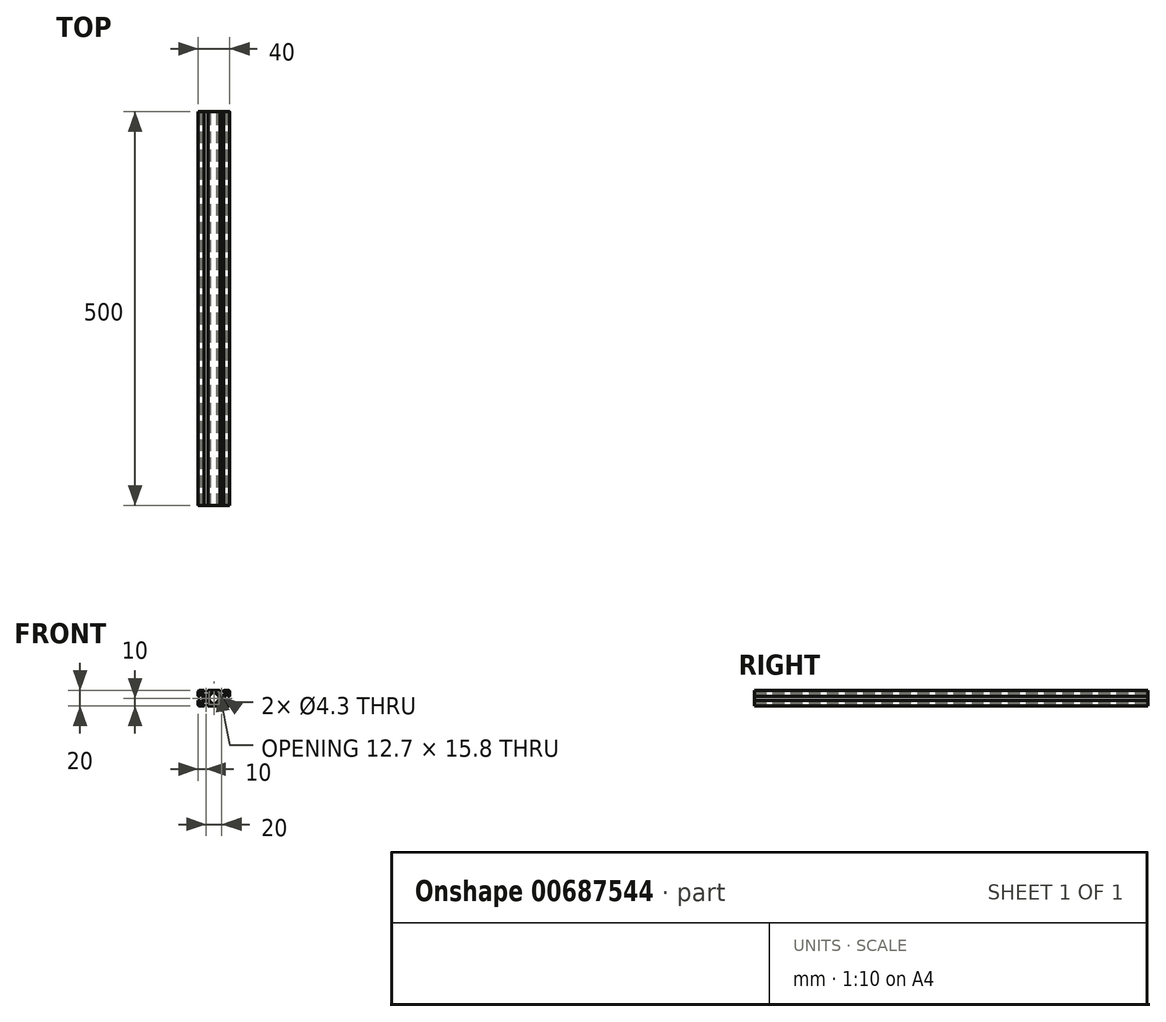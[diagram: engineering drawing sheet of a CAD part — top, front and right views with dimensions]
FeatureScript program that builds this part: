
annotation { "Feature Type Name" : "Feature", "Feature Type Description" : "" }
export const myFeature = defineFeature(function(context is Context, id is Id, definition is map)
    precondition{}
    {
        {
            var Q0;
            Q0=qCreatedBy(makeId("Front.planeOp"),FACE);
            var sketch = newSketch(context, id + "F0", { "sketchPlane" : qUnion([Q0])});
            skLineSegment(sketch, "E0", {"start": v(7.5, 9.2) * mm, "end": v(7.5, 8.5) * mm});
            skArc(sketch, "E1", {"start": v(7.2, 8.2) * mm, "mid": v(7.41, 8.29) * mm, "end": v(7.5, 8.5) * mm});
            skLineSegment(sketch, "E2", {"start": v(7.2, 8.2) * mm, "end": v(5, 8.2) * mm});
            skArc(sketch, "E3", {"start": v(5, 8.2) * mm, "mid": v(4.27, 7.7) * mm, "end": v(4.44, 6.83) * mm});
            skLineSegment(sketch, "E4", {"start": v(4.44, 6.83) * mm, "end": v(6.74, 4.53) * mm});
            skArc(sketch, "E5", {"start": v(6.74, 4.53) * mm, "mid": v(7.72, 3.88) * mm, "end": v(8.87, 3.65) * mm});
            skLineSegment(sketch, "E6", {"start": v(8.87, 3.65) * mm, "end": v(11.13, 3.65) * mm});
            skArc(sketch, "E7", {"start": v(11.13, 3.65) * mm, "mid": v(12.28, 3.88) * mm, "end": v(13.26, 4.53) * mm});
            skLineSegment(sketch, "E8", {"start": v(13.26, 4.53) * mm, "end": v(15.56, 6.83) * mm});
            skArc(sketch, "E9", {"start": v(15.56, 6.83) * mm, "mid": v(15.73, 7.7) * mm, "end": v(15, 8.2) * mm});
            skLineSegment(sketch, "E10", {"start": v(15, 8.2) * mm, "end": v(12.8, 8.2) * mm});
            skArc(sketch, "E11", {"start": v(12.5, 8.5) * mm, "mid": v(12.59, 8.29) * mm, "end": v(12.8, 8.2) * mm});
            skLineSegment(sketch, "E12", {"start": v(12.5, 8.5) * mm, "end": v(12.5, 9.2) * mm});
            skArc(sketch, "E13", {"start": v(13.3, 10) * mm, "mid": v(12.73, 9.77) * mm, "end": v(12.5, 9.2) * mm});
            skLineSegment(sketch, "E14", {"start": v(13.3, 10) * mm, "end": v(18, 10) * mm});
            skArc(sketch, "E15", {"start": v(20, 8) * mm, "mid": v(19.41, 9.41) * mm, "end": v(18, 10) * mm});
            skLineSegment(sketch, "E16", {"start": v(20, 8) * mm, "end": v(20, 3.3) * mm});
            skArc(sketch, "E17", {"start": v(19.2, 2.5) * mm, "mid": v(19.77, 2.73) * mm, "end": v(20, 3.3) * mm});
            skLineSegment(sketch, "E18", {"start": v(19.2, 2.5) * mm, "end": v(18.5, 2.5) * mm});
            skArc(sketch, "E19", {"start": v(18.2, 2.8) * mm, "mid": v(18.29, 2.59) * mm, "end": v(18.5, 2.5) * mm});
            skLineSegment(sketch, "E20", {"start": v(18.2, 2.8) * mm, "end": v(18.2, 5) * mm});
            skArc(sketch, "E21", {"start": v(18.2, 5) * mm, "mid": v(17.7, 5.73) * mm, "end": v(16.83, 5.56) * mm});
            skLineSegment(sketch, "E22", {"start": v(16.83, 5.56) * mm, "end": v(14.53, 3.26) * mm});
            skArc(sketch, "E23", {"start": v(14.53, 3.26) * mm, "mid": v(13.88, 2.28) * mm, "end": v(13.65, 1.13) * mm});
            skLineSegment(sketch, "E24", {"start": v(13.65, 1.13) * mm, "end": v(13.65, -1.13) * mm});
            skArc(sketch, "E25", {"start": v(13.65, -1.13) * mm, "mid": v(13.88, -2.28) * mm, "end": v(14.53, -3.26) * mm});
            skLineSegment(sketch, "E26", {"start": v(14.53, -3.26) * mm, "end": v(16.83, -5.56) * mm});
            skArc(sketch, "E27", {"start": v(16.83, -5.56) * mm, "mid": v(17.7, -5.73) * mm, "end": v(18.2, -5) * mm});
            skLineSegment(sketch, "E28", {"start": v(18.2, -5) * mm, "end": v(18.2, -2.8) * mm});
            skArc(sketch, "E29", {"start": v(18.5, -2.5) * mm, "mid": v(18.29, -2.59) * mm, "end": v(18.2, -2.8) * mm});
            skLineSegment(sketch, "E30", {"start": v(18.5, -2.5) * mm, "end": v(19.2, -2.5) * mm});
            skArc(sketch, "E31", {"start": v(20, -3.3) * mm, "mid": v(19.77, -2.73) * mm, "end": v(19.2, -2.5) * mm});
            skLineSegment(sketch, "E32", {"start": v(20, -3.3) * mm, "end": v(20, -8) * mm});
            skArc(sketch, "E33", {"start": v(18, -10) * mm, "mid": v(19.41, -9.41) * mm, "end": v(20, -8) * mm});
            skLineSegment(sketch, "E34", {"start": v(18, -10) * mm, "end": v(13.3, -10) * mm});
            skArc(sketch, "E35", {"start": v(12.5, -9.2) * mm, "mid": v(12.73, -9.77) * mm, "end": v(13.3, -10) * mm});
            skLineSegment(sketch, "E36", {"start": v(12.5, -9.2) * mm, "end": v(12.5, -8.5) * mm});
            skArc(sketch, "E37", {"start": v(12.8, -8.2) * mm, "mid": v(12.59, -8.29) * mm, "end": v(12.5, -8.5) * mm});
            skLineSegment(sketch, "E38", {"start": v(12.8, -8.2) * mm, "end": v(15, -8.2) * mm});
            skArc(sketch, "E39", {"start": v(15, -8.2) * mm, "mid": v(15.73, -7.7) * mm, "end": v(15.56, -6.83) * mm});
            skLineSegment(sketch, "E40", {"start": v(15.56, -6.83) * mm, "end": v(13.26, -4.53) * mm});
            skArc(sketch, "E41", {"start": v(13.26, -4.53) * mm, "mid": v(12.28, -3.88) * mm, "end": v(11.13, -3.65) * mm});
            skLineSegment(sketch, "E42", {"start": v(11.13, -3.65) * mm, "end": v(8.87, -3.65) * mm});
            skArc(sketch, "E43", {"start": v(8.87, -3.65) * mm, "mid": v(7.72, -3.88) * mm, "end": v(6.74, -4.53) * mm});
            skLineSegment(sketch, "E44", {"start": v(6.74, -4.53) * mm, "end": v(4.44, -6.83) * mm});
            skArc(sketch, "E45", {"start": v(4.44, -6.83) * mm, "mid": v(4.27, -7.7) * mm, "end": v(5, -8.2) * mm});
            skLineSegment(sketch, "E46", {"start": v(5, -8.2) * mm, "end": v(7.2, -8.2) * mm});
            skArc(sketch, "E47", {"start": v(7.5, -8.5) * mm, "mid": v(7.41, -8.29) * mm, "end": v(7.2, -8.2) * mm});
            skLineSegment(sketch, "E48", {"start": v(7.5, -8.5) * mm, "end": v(7.5, -9.2) * mm});
            skArc(sketch, "E49", {"start": v(6.7, -10) * mm, "mid": v(7.27, -9.77) * mm, "end": v(7.5, -9.2) * mm});
            skLineSegment(sketch, "E50", {"start": v(6.7, -10) * mm, "end": v(-6.7, -10) * mm});
            skArc(sketch, "E51", {"start": v(-7.5, -9.2) * mm, "mid": v(-7.27, -9.77) * mm, "end": v(-6.7, -10) * mm});
            skLineSegment(sketch, "E52", {"start": v(-7.5, -9.2) * mm, "end": v(-7.5, -8.5) * mm});
            skArc(sketch, "E53", {"start": v(-7.2, -8.2) * mm, "mid": v(-7.41, -8.29) * mm, "end": v(-7.5, -8.5) * mm});
            skLineSegment(sketch, "E54", {"start": v(-7.2, -8.2) * mm, "end": v(-5, -8.2) * mm});
            skArc(sketch, "E55", {"start": v(-5, -8.2) * mm, "mid": v(-4.27, -7.7) * mm, "end": v(-4.44, -6.83) * mm});
            skLineSegment(sketch, "E56", {"start": v(-4.44, -6.83) * mm, "end": v(-6.74, -4.53) * mm});
            skArc(sketch, "E57", {"start": v(-6.74, -4.53) * mm, "mid": v(-7.72, -3.88) * mm, "end": v(-8.87, -3.65) * mm});
            skLineSegment(sketch, "E58", {"start": v(-8.87, -3.65) * mm, "end": v(-11.13, -3.65) * mm});
            skArc(sketch, "E59", {"start": v(-11.13, -3.65) * mm, "mid": v(-12.28, -3.88) * mm, "end": v(-13.26, -4.53) * mm});
            skLineSegment(sketch, "E60", {"start": v(-13.26, -4.53) * mm, "end": v(-15.56, -6.83) * mm});
            skArc(sketch, "E61", {"start": v(-15.56, -6.83) * mm, "mid": v(-15.73, -7.7) * mm, "end": v(-15, -8.2) * mm});
            skLineSegment(sketch, "E62", {"start": v(-15, -8.2) * mm, "end": v(-12.8, -8.2) * mm});
            skArc(sketch, "E63", {"start": v(-12.5, -8.5) * mm, "mid": v(-12.59, -8.29) * mm, "end": v(-12.8, -8.2) * mm});
            skLineSegment(sketch, "E64", {"start": v(-12.5, -8.5) * mm, "end": v(-12.5, -9.2) * mm});
            skArc(sketch, "E65", {"start": v(-13.3, -10) * mm, "mid": v(-12.73, -9.77) * mm, "end": v(-12.5, -9.2) * mm});
            skLineSegment(sketch, "E66", {"start": v(-13.3, -10) * mm, "end": v(-18, -10) * mm});
            skArc(sketch, "E67", {"start": v(-20, -8) * mm, "mid": v(-19.41, -9.41) * mm, "end": v(-18, -10) * mm});
            skLineSegment(sketch, "E68", {"start": v(-20, -8) * mm, "end": v(-20, -3.3) * mm});
            skArc(sketch, "E69", {"start": v(-19.2, -2.5) * mm, "mid": v(-19.77, -2.73) * mm, "end": v(-20, -3.3) * mm});
            skLineSegment(sketch, "E70", {"start": v(-19.2, -2.5) * mm, "end": v(-18.5, -2.5) * mm});
            skArc(sketch, "E71", {"start": v(-18.2, -2.8) * mm, "mid": v(-18.29, -2.59) * mm, "end": v(-18.5, -2.5) * mm});
            skLineSegment(sketch, "E72", {"start": v(-18.2, -2.8) * mm, "end": v(-18.2, -5) * mm});
            skArc(sketch, "E73", {"start": v(-18.2, -5) * mm, "mid": v(-17.7, -5.73) * mm, "end": v(-16.83, -5.56) * mm});
            skLineSegment(sketch, "E74", {"start": v(-16.83, -5.56) * mm, "end": v(-14.53, -3.26) * mm});
            skArc(sketch, "E75", {"start": v(-14.53, -3.26) * mm, "mid": v(-13.88, -2.28) * mm, "end": v(-13.65, -1.13) * mm});
            skLineSegment(sketch, "E76", {"start": v(-13.65, -1.13) * mm, "end": v(-13.65, 1.13) * mm});
            skArc(sketch, "E77", {"start": v(-13.65, 1.13) * mm, "mid": v(-13.88, 2.28) * mm, "end": v(-14.53, 3.26) * mm});
            skLineSegment(sketch, "E78", {"start": v(-14.53, 3.26) * mm, "end": v(-16.83, 5.56) * mm});
            skArc(sketch, "E79", {"start": v(-16.83, 5.56) * mm, "mid": v(-17.7, 5.73) * mm, "end": v(-18.2, 5) * mm});
            skLineSegment(sketch, "E80", {"start": v(-18.2, 5) * mm, "end": v(-18.2, 2.8) * mm});
            skArc(sketch, "E81", {"start": v(-18.5, 2.5) * mm, "mid": v(-18.29, 2.59) * mm, "end": v(-18.2, 2.8) * mm});
            skLineSegment(sketch, "E82", {"start": v(-18.5, 2.5) * mm, "end": v(-19.2, 2.5) * mm});
            skArc(sketch, "E83", {"start": v(-20, 3.3) * mm, "mid": v(-19.77, 2.73) * mm, "end": v(-19.2, 2.5) * mm});
            skLineSegment(sketch, "E84", {"start": v(-20, 3.3) * mm, "end": v(-20, 8) * mm});
            skArc(sketch, "E85", {"start": v(-18, 10) * mm, "mid": v(-19.41, 9.41) * mm, "end": v(-20, 8) * mm});
            skLineSegment(sketch, "E86", {"start": v(-18, 10) * mm, "end": v(-13.3, 10) * mm});
            skArc(sketch, "E87", {"start": v(-12.5, 9.2) * mm, "mid": v(-12.73, 9.77) * mm, "end": v(-13.3, 10) * mm});
            skLineSegment(sketch, "E88", {"start": v(-12.5, 9.2) * mm, "end": v(-12.5, 8.5) * mm});
            skArc(sketch, "E89", {"start": v(-12.8, 8.2) * mm, "mid": v(-12.59, 8.29) * mm, "end": v(-12.5, 8.5) * mm});
            skLineSegment(sketch, "E90", {"start": v(-12.8, 8.2) * mm, "end": v(-15, 8.2) * mm});
            skArc(sketch, "E91", {"start": v(-15, 8.2) * mm, "mid": v(-15.73, 7.7) * mm, "end": v(-15.56, 6.83) * mm});
            skLineSegment(sketch, "E92", {"start": v(-15.56, 6.83) * mm, "end": v(-13.26, 4.53) * mm});
            skArc(sketch, "E93", {"start": v(-13.26, 4.53) * mm, "mid": v(-12.28, 3.88) * mm, "end": v(-11.13, 3.65) * mm});
            skLineSegment(sketch, "E94", {"start": v(-11.13, 3.65) * mm, "end": v(-8.87, 3.65) * mm});
            skArc(sketch, "E95", {"start": v(-8.87, 3.65) * mm, "mid": v(-7.72, 3.88) * mm, "end": v(-6.74, 4.53) * mm});
            skLineSegment(sketch, "E96", {"start": v(-6.74, 4.53) * mm, "end": v(-4.44, 6.83) * mm});
            skArc(sketch, "E97", {"start": v(-4.44, 6.83) * mm, "mid": v(-4.27, 7.7) * mm, "end": v(-5, 8.2) * mm});
            skLineSegment(sketch, "E98", {"start": v(-5, 8.2) * mm, "end": v(-7.2, 8.2) * mm});
            skArc(sketch, "E99", {"start": v(-7.5, 8.5) * mm, "mid": v(-7.41, 8.29) * mm, "end": v(-7.2, 8.2) * mm});
            skLineSegment(sketch, "E100", {"start": v(-7.5, 8.5) * mm, "end": v(-7.5, 9.2) * mm});
            skArc(sketch, "E101", {"start": v(-6.7, 10) * mm, "mid": v(-7.27, 9.77) * mm, "end": v(-7.5, 9.2) * mm});
            skLineSegment(sketch, "E102", {"start": v(-6.7, 10) * mm, "end": v(6.7, 10) * mm});
            skArc(sketch, "E103", {"start": v(7.5, 9.2) * mm, "mid": v(7.27, 9.77) * mm, "end": v(6.7, 10) * mm});
            skCircle(sketch, "E104", {"center": v(10, 0) * mm, "radius": 2.15 * mm});
            skCircle(sketch, "E105", {"center": v(-10, 0) * mm, "radius": 2.15 * mm});
            skArc(sketch, "E106", {"start": v(1.41, 7.31) * mm, "mid": v(0, 7.9) * mm, "end": v(-1.41, 7.31) * mm});
            skLineSegment(sketch, "E107", {"start": v(-1.41, 7.31) * mm, "end": v(-5.47, 3.26) * mm});
            skArc(sketch, "E108", {"start": v(-5.47, 3.26) * mm, "mid": v(-6.12, 2.28) * mm, "end": v(-6.35, 1.13) * mm});
            skLineSegment(sketch, "E109", {"start": v(-6.35, 1.13) * mm, "end": v(-6.35, -1.13) * mm});
            skArc(sketch, "E110", {"start": v(-6.35, -1.13) * mm, "mid": v(-6.12, -2.28) * mm, "end": v(-5.47, -3.26) * mm});
            skLineSegment(sketch, "E111", {"start": v(-5.47, -3.26) * mm, "end": v(-1.41, -7.31) * mm});
            skArc(sketch, "E112", {"start": v(-1.41, -7.31) * mm, "mid": v(0, -7.9) * mm, "end": v(1.41, -7.31) * mm});
            skLineSegment(sketch, "E113", {"start": v(1.41, -7.31) * mm, "end": v(5.47, -3.26) * mm});
            skArc(sketch, "E114", {"start": v(5.47, -3.26) * mm, "mid": v(6.12, -2.28) * mm, "end": v(6.35, -1.13) * mm});
            skLineSegment(sketch, "E115", {"start": v(6.35, -1.13) * mm, "end": v(6.35, 1.13) * mm});
            skArc(sketch, "E116", {"start": v(6.35, 1.13) * mm, "mid": v(6.12, 2.28) * mm, "end": v(5.47, 3.26) * mm});
            skLineSegment(sketch, "E117", {"start": v(5.47, 3.26) * mm, "end": v(1.41, 7.31) * mm});
            skSolve(sketch);
        }
        {
            var Q0;
            Q0=makeQuery(id+"F0.imprint","IMPRINT",FACE,{"disambiguationData":[TD([[makeQuery(id+"F0.imprint","IMPRINT",EDGE,{"derivedFrom":sQuery(id+"F0.wireOp",EDGE,"E0")}),-1.0]])]});
            extrude(context, id + "F1", {"entities" : qUnion([Q0]), "depth" : 500 * mm, "offsetDistance" : 25 * mm, "symmetric" : true});
        }
    });
